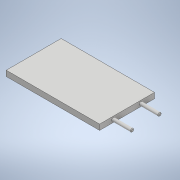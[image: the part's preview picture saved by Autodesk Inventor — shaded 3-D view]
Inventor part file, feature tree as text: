
AUTODESK INVENTOR PART (.ipt)
format: ipt  version: 2022 (Build 260153000, 153)  size: 121,856 bytes
history: native  units: mm
features: extrude x4, sketch x4, chamfer x2
ambient origin geometry x8: Origin, YZ Plane, XZ Plane, XY Plane, X Axis, Y Axis, Z Axis, Center Point
bodies: Solid1 (feature_tree)
feature tree (10):
  extrude  "Extrusion1"  Depth=1000.0mm
  extrude  "Extrusion2"  Depth=32.5mm
  extrude  "Extrusion3"  Depth=60.0mm TaperAngle=0.0deg
  extrude  "Extrusion4"  Depth=60.0mm
  chamfer  "Chamfer1"  Distance=350.0mm
  chamfer  "Chamfer2"  Distance=60.0mm
  sketch  "Sketch1"  dims[d0=1700.0mm d1=1000.0mm]
  sketch  "Sketch2"  dims[d2=100.0mm d3=0.0mm d4=32.5mm]
  sketch  "Sketch3"  dims[d5=32.5mm d6=60.0mm d7=0.0mm]
  sketch  "Sketch4"  dims[d8=60.0mm d9=60.0mm d10=350.0mm d11=0.0mm d12=60.0mm d13=350.0mm d14=0.0mm d15=10.0mm d16=2.0mm d17=45.0deg d18=10.0mm d19=2.0mm d20=45.0deg]
